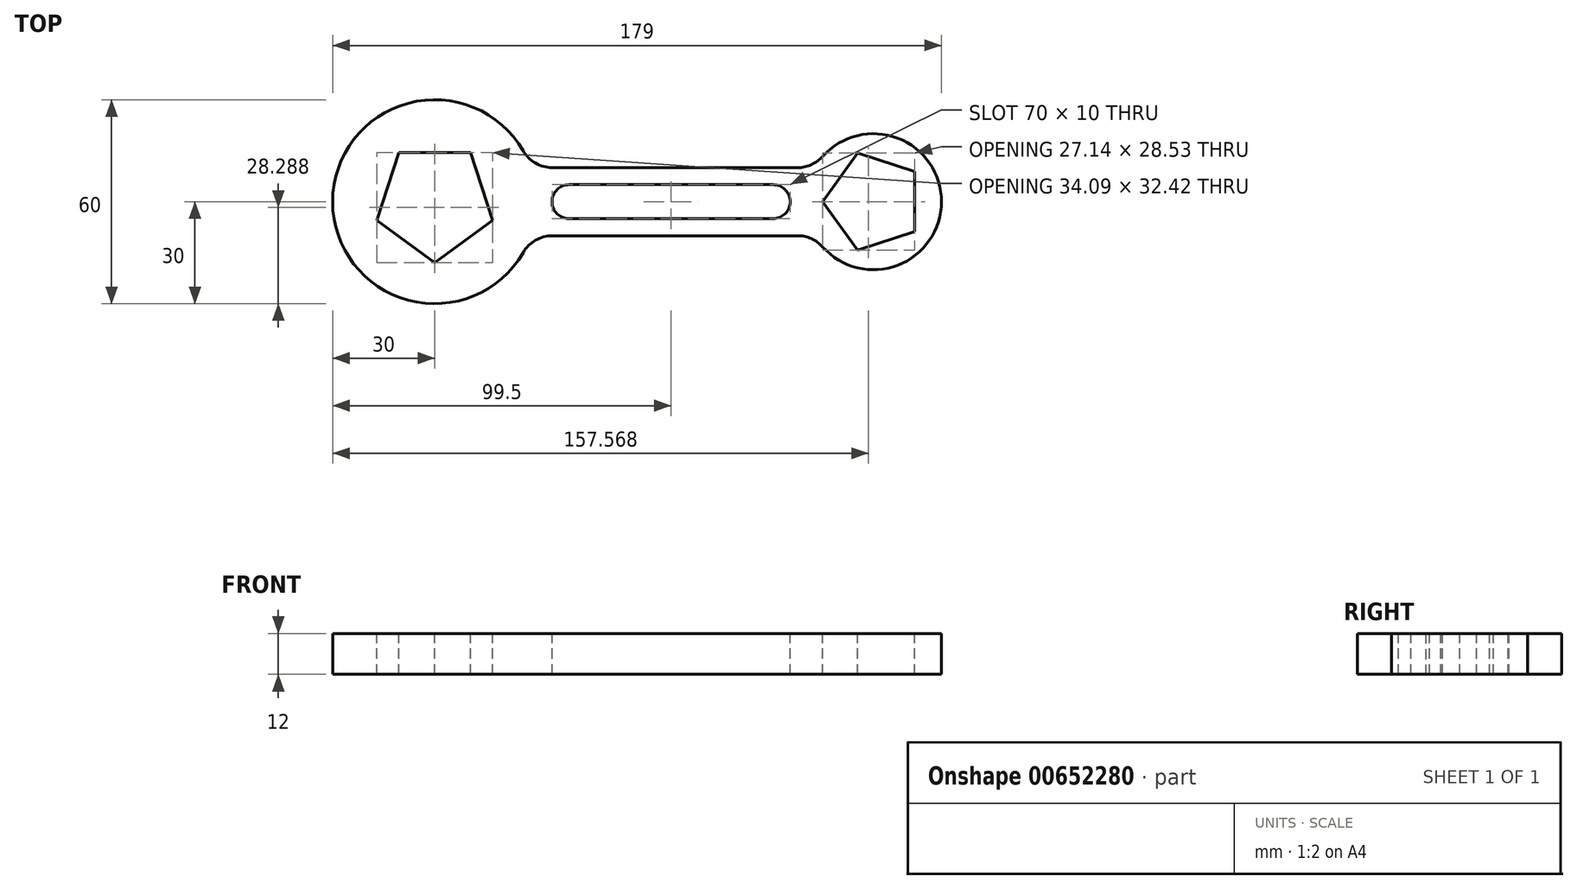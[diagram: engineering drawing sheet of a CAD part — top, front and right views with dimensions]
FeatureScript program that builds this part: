
annotation { "Feature Type Name" : "Feature", "Feature Type Description" : "" }
export const myFeature = defineFeature(function(context is Context, id is Id, definition is map)
    precondition{}
    {
        {
            var Q0;
            Q0=qCreatedBy(makeId("Top.planeOp"),FACE);
            var sketch = newSketch(context, id + "F0", { "sketchPlane" : qUnion([Q0])});
            skCircle(sketch, "E0", {"center": v(-64.5, 0) * mm, "radius": 30 * mm});
            skCircle(sketch, "E1", {"center": v(64.5, 0) * mm, "radius": 20 * mm});
            skLineSegment(sketch, "E2.bottom", {"start": v(64.5, -10) * mm, "end": v(-64.5, -10) * mm});
            skLineSegment(sketch, "E2.top", {"start": v(64.5, 10) * mm, "end": v(-64.5, 10) * mm});
            skLineSegment(sketch, "E2.left", {"start": v(64.5, -10) * mm, "end": v(64.5, 10) * mm});
            skLineSegment(sketch, "E2.right", {"start": v(-64.5, -10) * mm, "end": v(-64.5, 10) * mm});
            skPoint(sketch, "E2.middle", {"position": v(0, 0) * mm});
            skSolve(sketch);
        }
        {
            var Q0;
            Q0 = qSketchRegion(id + "F0", true);
            extrude(context, id + "F1", {"entities" : qUnion([Q0]), "depth" : 12 * mm, "offsetDistance" : 25 * mm});
        }
        {
            var Q0;
            Q0=makeQuery(id+"F1.opExtrude","CAP_FACE",FACE,{"disambiguationData":[OSD([sQuery(id+"F0.wireOp",EDGE,"E0"),sQuery(id+"F0.wireOp",EDGE,"E1"),sQuery(id+"F0.wireOp",EDGE,"E2.bottom"),sQuery(id+"F0.wireOp",EDGE,"E2.top")])],"isStart":false});
            var sketch = newSketch(context, id + "F2", { "sketchPlane" : qUnion([Q0])});
            skCircle(sketch, "E3.cCircle", {"center": v(64.5, 0) * mm, "radius": 15 * mm, "construction": true});
            skLineSegment(sketch, "E3.0", {"start": v(76.64, -8.82) * mm, "end": v(59.86, -14.27) * mm});
            skLineSegment(sketch, "E3.1", {"start": v(59.86, -14.27) * mm, "end": v(49.5, 0) * mm});
            skLineSegment(sketch, "E3.2", {"start": v(49.5, 0) * mm, "end": v(59.86, 14.27) * mm});
            skLineSegment(sketch, "E3.3", {"start": v(59.86, 14.27) * mm, "end": v(76.64, 8.82) * mm});
            skLineSegment(sketch, "E3.4", {"start": v(76.64, 8.82) * mm, "end": v(76.64, -8.82) * mm});
            skCircle(sketch, "E4.cCircle", {"center": v(-64.5, 0) * mm, "radius": 17.92 * mm, "construction": true});
            skLineSegment(sketch, "E4.0", {"start": v(-64.5, -17.92) * mm, "end": v(-81.55, -5.54) * mm});
            skLineSegment(sketch, "E4.1", {"start": v(-81.55, -5.54) * mm, "end": v(-75.04, 14.5) * mm});
            skLineSegment(sketch, "E4.2", {"start": v(-75.04, 14.5) * mm, "end": v(-53.96, 14.5) * mm});
            skLineSegment(sketch, "E4.3", {"start": v(-53.96, 14.5) * mm, "end": v(-47.45, -5.54) * mm});
            skLineSegment(sketch, "E4.4", {"start": v(-47.45, -5.54) * mm, "end": v(-64.5, -17.92) * mm});
            skSolve(sketch);
        }
        {
            var Q0;
            Q0=makeQuery(id+"F2.imprint","IMPRINT",FACE,{"disambiguationData":[TD([[makeQuery(id+"F2.imprint","IMPRINT",EDGE,{"derivedFrom":sQuery(id+"F2.wireOp",EDGE,"E4.0")}),-1.0]])]});
            var Q1;
            Q1=makeQuery(id+"F2.imprint","IMPRINT",FACE,{"disambiguationData":[TD([[makeQuery(id+"F2.imprint","IMPRINT",EDGE,{"derivedFrom":sQuery(id+"F2.wireOp",EDGE,"E3.0")}),-1.0]])]});
            extrude(context, id + "F3", {"entities" : qUnion([Q0, Q1]), "operationType" : NewBodyOperationType.REMOVE, "oppositeDirection" : true, "depth" : 25 * mm, "offsetDistance" : 25 * mm});
        }
        {
            var Q0;
            Q0=makeQuery(id+"F1.opExtrude","CAP_FACE",FACE,{"disambiguationData":[OSD([sQuery(id+"F0.wireOp",EDGE,"E0"),sQuery(id+"F0.wireOp",EDGE,"E1"),sQuery(id+"F0.wireOp",EDGE,"E2.bottom"),sQuery(id+"F0.wireOp",EDGE,"E2.top")])],"isStart":false});
            var sketch = newSketch(context, id + "F4", { "sketchPlane" : qUnion([Q0])});
            skLineSegment(sketch, "E5.bottom", {"start": v(-25, 5) * mm, "end": v(35, 5) * mm});
            skLineSegment(sketch, "E5.top", {"start": v(-25, -5) * mm, "end": v(35, -5) * mm});
            skLineSegment(sketch, "E5.left", {"start": v(-25, 5) * mm, "end": v(-25, -5) * mm});
            skLineSegment(sketch, "E5.right", {"start": v(35, 5) * mm, "end": v(35, -5) * mm});
            skCircle(sketch, "E6", {"center": v(-25, 0) * mm, "radius": 5 * mm});
            skCircle(sketch, "E7", {"center": v(35, 0) * mm, "radius": 5 * mm});
            skSolve(sketch);
        }
        {
            var Q0;
            {var subQ0=sQuery(id+"F4.wireOp",EDGE,"E5.left");Q0=makeQuery(id+"F4.imprint","IMPRINT",FACE,{"disambiguationData":[TD([[makeQuery(id+"F4.imprint","IMPRINT",EDGE,{"derivedFrom":subQ0}),-1.0]])]});}
            var Q1;
            {var subQ0=sQuery(id+"F4.wireOp",EDGE,"E5.bottom");Q1=makeQuery(id+"F4.imprint","IMPRINT",FACE,{"disambiguationData":[TD([[makeQuery(id+"F4.imprint","IMPRINT",EDGE,{"derivedFrom":subQ0}),-1.0]])]});}
            var Q2;
            {var subQ0=sQuery(id+"F4.wireOp",EDGE,"E5.left");Q2=makeQuery(id+"F4.imprint","IMPRINT",FACE,{"disambiguationData":[TD([[makeQuery(id+"F4.imprint","IMPRINT",EDGE,{"derivedFrom":subQ0}),1.0]])]});}
            var Q3;
            {var subQ0=sQuery(id+"F4.wireOp",EDGE,"E5.right");Q3=makeQuery(id+"F4.imprint","IMPRINT",FACE,{"disambiguationData":[TD([[makeQuery(id+"F4.imprint","IMPRINT",EDGE,{"derivedFrom":subQ0}),-1.0]])]});}
            var Q4;
            {var subQ0=sQuery(id+"F4.wireOp",EDGE,"E5.right");Q4=makeQuery(id+"F4.imprint","IMPRINT",FACE,{"disambiguationData":[TD([[makeQuery(id+"F4.imprint","IMPRINT",EDGE,{"derivedFrom":subQ0}),1.0]])]});}
            extrude(context, id + "F5", {"entities" : qUnion([Q0, Q1, Q2, Q3, Q4]), "operationType" : NewBodyOperationType.REMOVE, "oppositeDirection" : true, "depth" : 25 * mm, "offsetDistance" : 25 * mm});
        }
        {
            var Q0;
            Q0=makeQuery(id+"F1.opExtrude","SWEPT_EDGE",EDGE,{"disambiguationData":[OSD([sQuery(id+"F0.wireOp",EDGE,"E0"),sQuery(id+"F0.wireOp",EDGE,"E2.top")])]});
            var Q1;
            Q1=makeQuery(id+"F1.opExtrude","SWEPT_EDGE",EDGE,{"disambiguationData":[OSD([sQuery(id+"F0.wireOp",EDGE,"E0"),sQuery(id+"F0.wireOp",EDGE,"E2.bottom")])]});
            var Q2;
            Q2=makeQuery(id+"F1.opExtrude","SWEPT_EDGE",EDGE,{"disambiguationData":[OSD([sQuery(id+"F0.wireOp",EDGE,"E1"),sQuery(id+"F0.wireOp",EDGE,"E2.bottom")])]});
            var Q3;
            Q3=makeQuery(id+"F1.opExtrude","SWEPT_EDGE",EDGE,{"disambiguationData":[OSD([sQuery(id+"F0.wireOp",EDGE,"E1"),sQuery(id+"F0.wireOp",EDGE,"E2.top")])]});
            fillet(context, id + "F6", {"entities" : qUnion([Q0, Q1, Q2, Q3]), "radius" : 10 * mm, "tangentPropagation" : true, "allowEdgeOverflow" : false});
        }
    });
